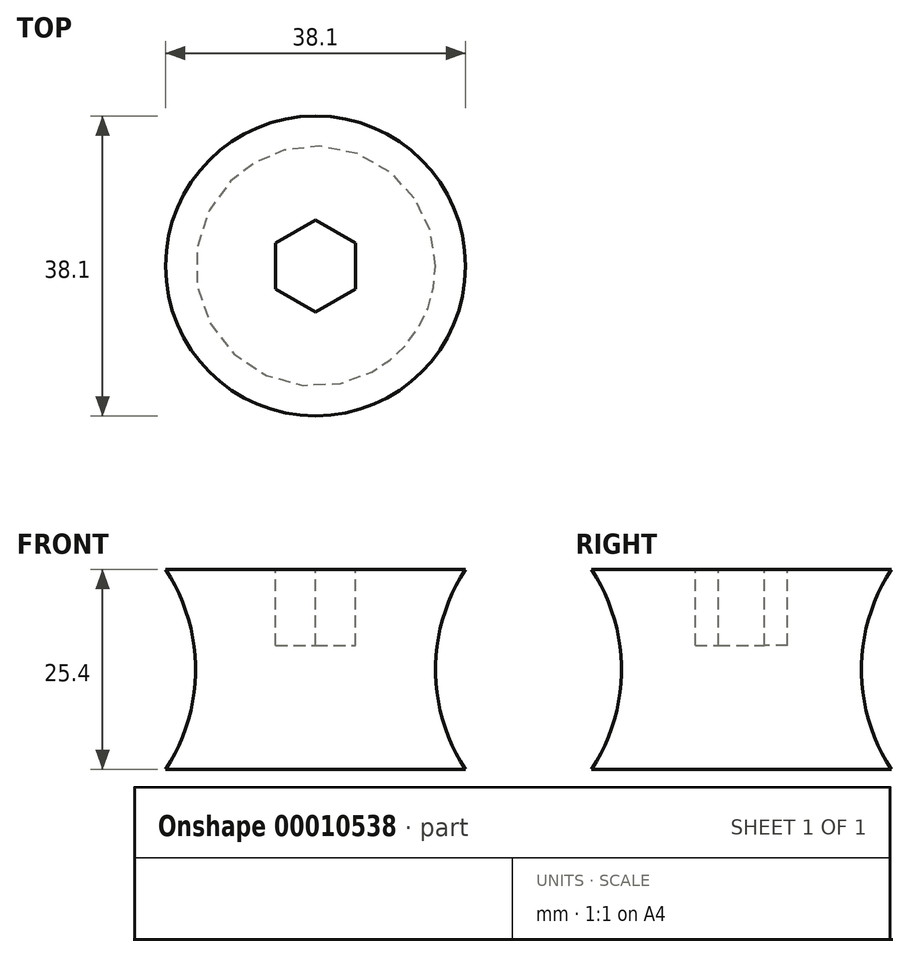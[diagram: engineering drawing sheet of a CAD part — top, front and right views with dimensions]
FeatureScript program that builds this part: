
annotation { "Feature Type Name" : "Feature", "Feature Type Description" : "" }
export const myFeature = defineFeature(function(context is Context, id is Id, definition is map)
    precondition{}
    {
        {
            var Q0;
            Q0=qCreatedBy(makeId("Right.planeOp"),FACE);
            var sketch = newSketch(context, id + "F0", { "sketchPlane" : qUnion([Q0])});
            skLineSegment(sketch, "E0", {"start": v(0, 25.4) * mm, "end": v(19.05, 25.4) * mm});
            skArc(sketch, "E1", {"start": v(19.05, 25.4) * mm, "mid": v(15.24, 12.7) * mm, "end": v(19.05, 0) * mm});
            skLineSegment(sketch, "E2", {"start": v(19.05, 0) * mm, "end": v(0, 0) * mm});
            skLineSegment(sketch, "E3", {"start": v(0, 25.4) * mm, "end": v(0, 0) * mm});
            skSolve(sketch);
        }
        {
            var Q0;
            Q0 = qSketchRegion(id + "F0", true);
            var Q1;
            Q1=sQuery(id+"F0.wireOp",EDGE,"E0");
            var Q2;
            Q2=sQuery(id+"F0.wireOp",EDGE,"E1");
            var Q3;
            Q3=sQuery(id+"F0.wireOp",EDGE,"E2");
            var Q4;
            Q4=sQuery(id+"F0.wireOp",EDGE,"E3");
            revolve(context, id + "F1", {"entities" : qUnion([Q0]), "surfaceEntities" : qUnion([Q1, Q2, Q3]), "axis" : qUnion([Q4]), "revolveType" : RevolveType.FULL});
        }
        {
            var Q0;
            Q0=makeQuery(id+"F1.opRevolve","SWEPT_FACE",FACE,{"disambiguationData":[OSD([sQuery(id+"F0.wireOp",EDGE,"E0")])]});
            var sketch = newSketch(context, id + "F2", { "sketchPlane" : qUnion([Q0])});
            skCircle(sketch, "E4.cCircle", {"center": v(0, 0) * mm, "radius": 5.08 * mm, "construction": true});
            skLineSegment(sketch, "E4.0", {"start": v(0, 5.87) * mm, "end": v(5.08, 2.93) * mm});
            skLineSegment(sketch, "E4.1", {"start": v(5.08, 2.93) * mm, "end": v(5.08, -2.93) * mm});
            skLineSegment(sketch, "E4.2", {"start": v(5.08, -2.93) * mm, "end": v(0, -5.87) * mm});
            skLineSegment(sketch, "E4.3", {"start": v(0, -5.87) * mm, "end": v(-5.08, -2.93) * mm});
            skLineSegment(sketch, "E4.4", {"start": v(-5.08, -2.93) * mm, "end": v(-5.08, 2.93) * mm});
            skLineSegment(sketch, "E4.5", {"start": v(-5.08, 2.93) * mm, "end": v(0, 5.87) * mm});
            skPoint(sketch, "E4.0.midPoint", {"position": v(2.54, 4.4) * mm});
            skSolve(sketch);
        }
        {
            var Q0;
            Q0 = qSketchRegion(id + "F2", true);
            extrude(context, id + "F3", {"entities" : qUnion([Q0]), "operationType" : NewBodyOperationType.REMOVE, "oppositeDirection" : true, "depth" : 9.65 * mm});
        }
    });
